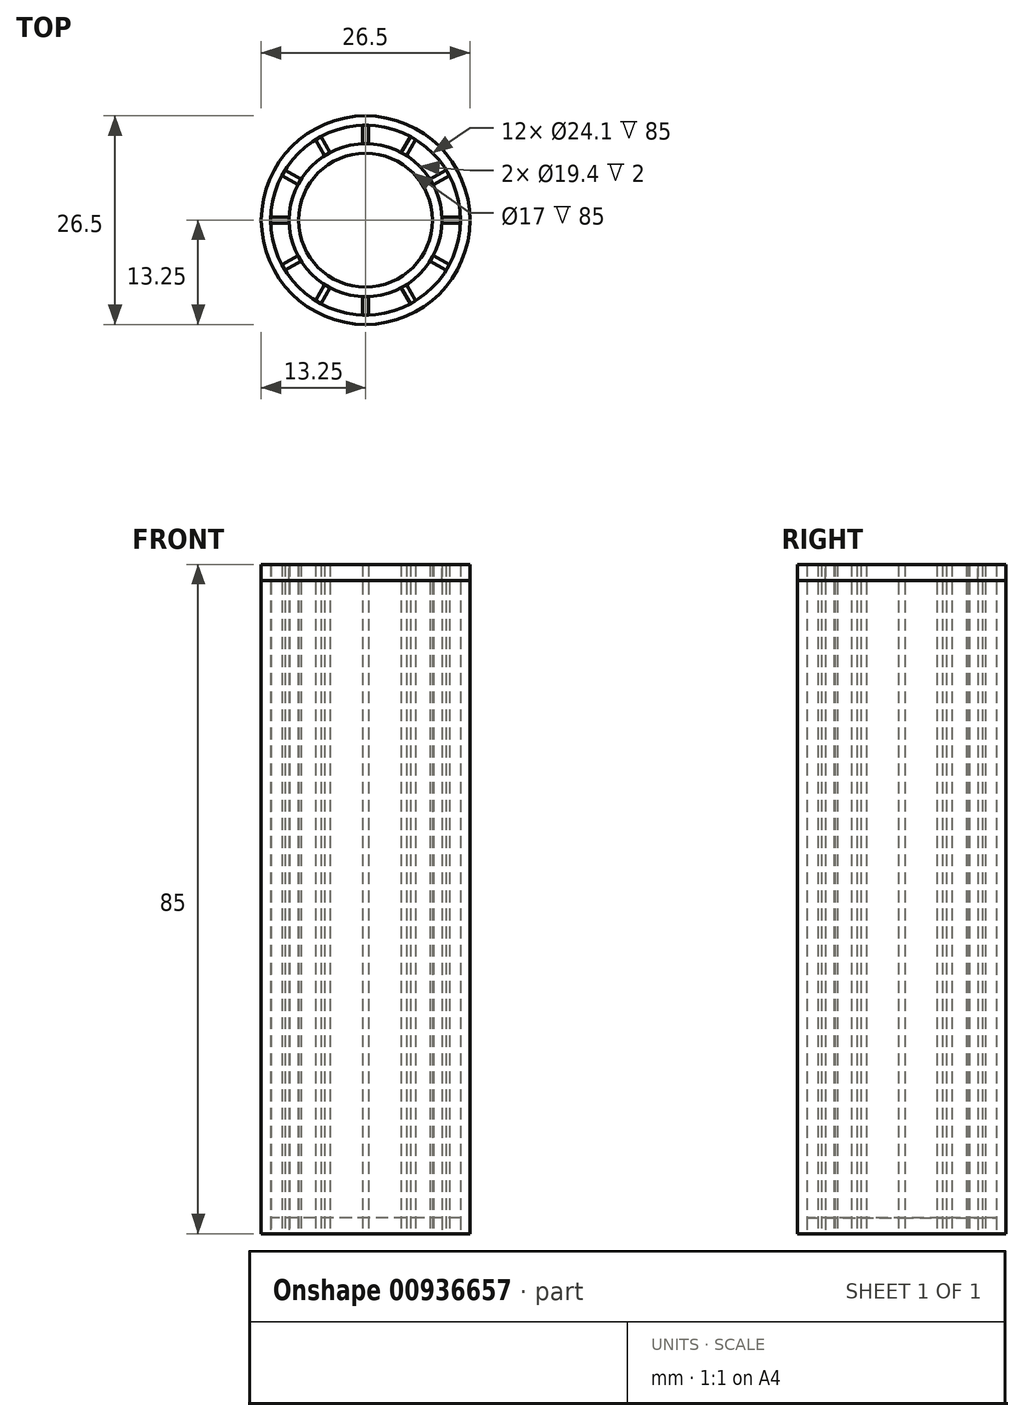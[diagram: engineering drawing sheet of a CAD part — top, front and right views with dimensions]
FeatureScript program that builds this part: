
annotation { "Feature Type Name" : "Feature", "Feature Type Description" : "" }
export const myFeature = defineFeature(function(context is Context, id is Id, definition is map)
    precondition{}
    {
        {
            var Q0;
            Q0=qCreatedBy(makeId("Top.planeOp"),FACE);
            var sketch = newSketch(context, id + "F0", { "sketchPlane" : qUnion([Q0])});
            skCircle(sketch, "E0", {"center": v(0, 0) * mm, "radius": 8.5 * mm});
            skCircle(sketch, "E1", {"center": v(0, 0) * mm, "radius": 13.25 * mm});
            skCircle(sketch, "E2", {"center": v(0, 0) * mm, "radius": 9.7 * mm});
            skCircle(sketch, "E3", {"center": v(0, 0) * mm, "radius": 12.05 * mm});
            skLineSegment(sketch, "E4", {"start": v(0, -9.7) * mm, "end": v(0, -12.05) * mm, "construction": true});
            skLineSegment(sketch, "E5", {"start": v(0.4, -9.7) * mm, "end": v(0.4, -12.04) * mm});
            skLineSegment(sketch, "E6.MirrorCS", {"start": v(-0.4, -9.7) * mm, "end": v(-0.4, -12.04) * mm});
            skSolve(sketch);
        }
        {
            assignVariable(context, id + "F1", {"name" : "height", "anyValue" : 85});
        }
        {
            var Q0;
            Q0=makeQuery(id+"F0.imprint","IMPRINT",FACE,{"disambiguationData":[TD([[makeQuery(id+"F0.imprint","IMPRINT",EDGE,{"derivedFrom":sQuery(id+"F0.wireOp",EDGE,"E0")}),-1.0]])]});
            var Q1;
            Q1=makeQuery(id+"F0.imprint","IMPRINT",FACE,{"disambiguationData":[TD([[makeQuery(id+"F0.imprint","IMPRINT",EDGE,{"derivedFrom":sQuery(id+"F0.wireOp",EDGE,"E1")}),1.0]])]});
            extrude(context, id + "F2", {"entities" : qUnion([Q0, Q1]), "depth" : (getVariable(context, 'height')) * mm, "offsetDistance" : 25 * mm});
        }
        {
            var Q0;
            {var subQ0=sQuery(id+"F0.wireOp",EDGE,"E5");Q0=makeQuery(id+"F0.imprint","IMPRINT",FACE,{"disambiguationData":[TD([[makeQuery(id+"F0.imprint","IMPRINT",EDGE,{"derivedFrom":subQ0}),1.0]])]});}
            var Q1;
            {var subQ0=sQuery(id+"F0.wireOp",EDGE,"E5");Q1=makeQuery(id+"F0.imprint","IMPRINT",FACE,{"disambiguationData":[TD([[makeQuery(id+"F0.imprint","IMPRINT",EDGE,{"derivedFrom":subQ0}),-1.0]])]});}
            extrude(context, id + "F3", {"entities" : qUnion([Q0, Q1]), "depth" : 2 * mm, "offsetDistance" : 25 * mm});
        }
        {
            var Q0;
            {var subQ0=sQuery(id+"F0.wireOp",EDGE,"E5");Q0=makeQuery(id+"F0.imprint","IMPRINT",FACE,{"disambiguationData":[TD([[makeQuery(id+"F0.imprint","IMPRINT",EDGE,{"derivedFrom":subQ0}),-1.0]])]});}
            extrude(context, id + "F4", {"entities" : qUnion([Q0]), "depth" : (getVariable(context, 'height')) * mm, "offsetDistance" : 25 * mm});
        }
        {
            var Q0;
            Q0=makeQuery(id+"F4.opExtrude","SWEPT_BODY",BODY,{"disambiguationData":[OSD([sQuery(id+"F0.wireOp",EDGE,"E2"),sQuery(id+"F0.wireOp",EDGE,"E3"),sQuery(id+"F0.wireOp",EDGE,"E5"),sQuery(id+"F0.wireOp",EDGE,"E6.MirrorCS")])]});
            var Q1;
            Q1=makeQuery(id+"F2.opExtrude","SWEPT_BODY",BODY,{"disambiguationData":[OSD([sQuery(id+"F0.wireOp",EDGE,"E1"),sQuery(id+"F0.wireOp",EDGE,"E3")])]});
            var Q2;
            Q2=makeQuery(id+"F2.opExtrude","SWEPT_FACE",FACE,{"disambiguationData":[OSD([sQuery(id+"F0.wireOp",EDGE,"E0")])]});
            circularPattern(context, id + "F5", {"entities" : qUnion([Q0, Q1]), "axis" : qUnion([Q2]), "angle" : 360 * degree, "instanceCount" : 12, "equalSpace" : true});
        }
        {
            var Q0;
            Q0=makeQuery(id+"F2.opExtrude","CAP_FACE",FACE,{"disambiguationData":[OSD([sQuery(id+"F0.wireOp",EDGE,"E0"),sQuery(id+"F0.wireOp",EDGE,"E2")])],"isStart":false});
            var sketch = newSketch(context, id + "F6", { "sketchPlane" : qUnion([Q0])});
            skCircle(sketch, "E7", {"center": v(0, 0) * mm, "radius": 8.5 * mm});
            skCircle(sketch, "E8", {"center": v(0, 0) * mm, "radius": 13.25 * mm});
            skSolve(sketch);
        }
        {
            var Q0;
            Q0=makeQuery(id+"F6.imprint","IMPRINT",FACE,{"disambiguationData":[TD([[makeQuery(id+"F6.imprint","IMPRINT",EDGE,{"derivedFrom":sQuery(id+"F6.wireOp",EDGE,"E8")}),1.0]])]});
            extrude(context, id + "F7", {"entities" : qUnion([Q0]), "oppositeDirection" : true, "depth" : 2 * mm, "offsetDistance" : 25 * mm});
        }
    });
